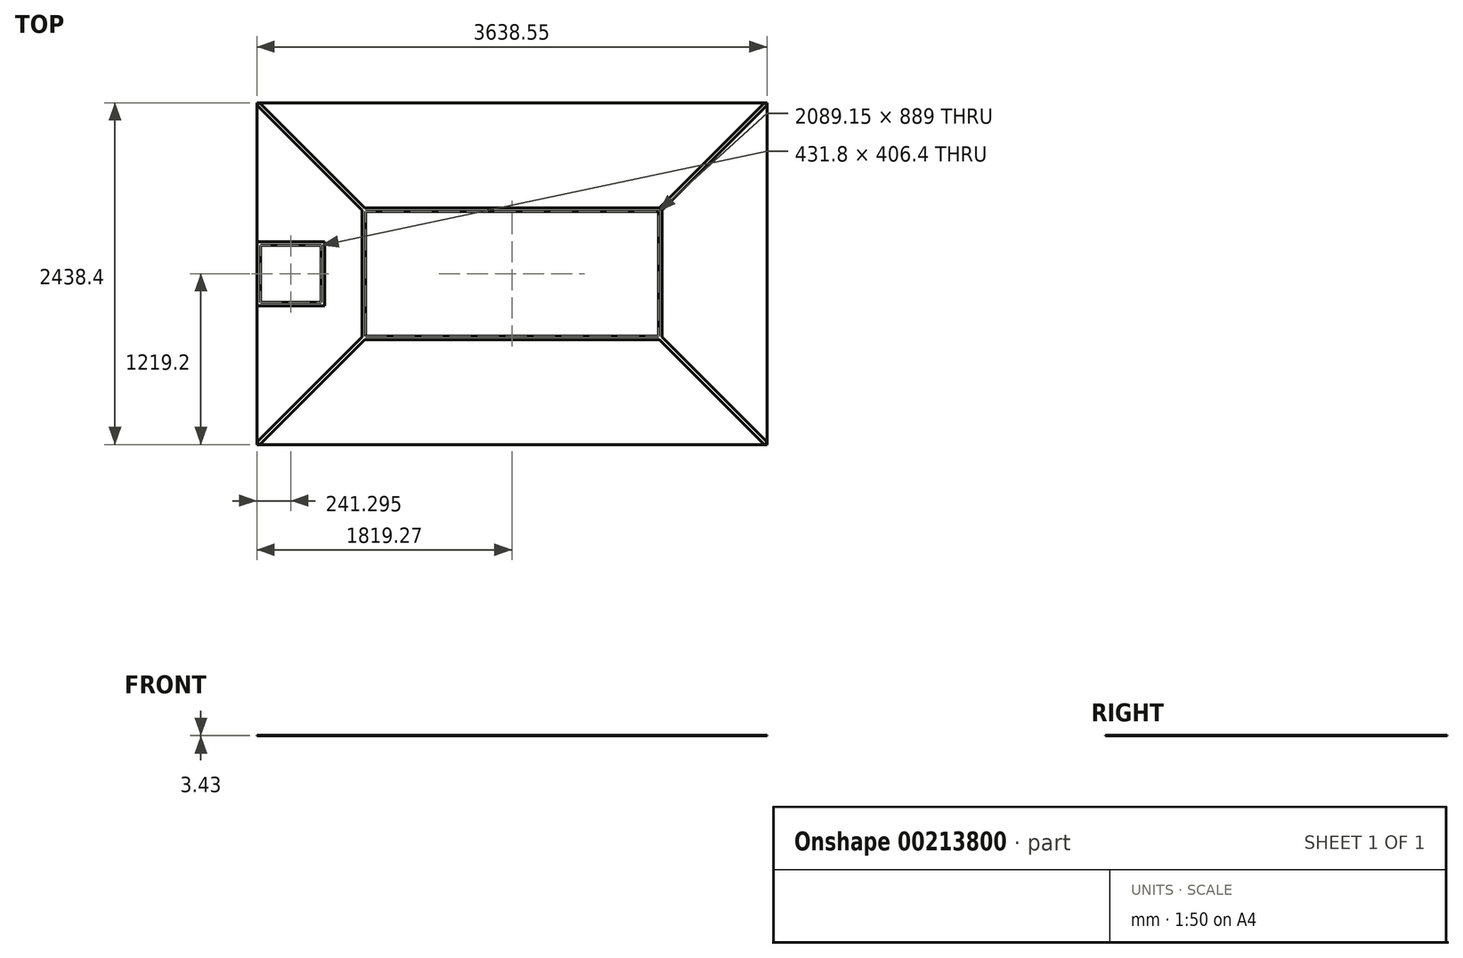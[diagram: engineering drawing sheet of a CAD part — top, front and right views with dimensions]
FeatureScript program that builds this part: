
annotation { "Feature Type Name" : "Feature", "Feature Type Description" : "" }
export const myFeature = defineFeature(function(context is Context, id is Id, definition is map)
    precondition{}
    {
        {
            var Q0;
            Q0=qCreatedBy(makeId("Top.planeOp"),FACE);
            var sketch = newSketch(context, id + "F0", { "sketchPlane" : qUnion([Q0])});
            skLineSegment(sketch, "E0.bottom", {"start": v(1819.27, 1219.2) * mm, "end": v(-1819.28, 1219.2) * mm});
            skLineSegment(sketch, "E0.top", {"start": v(1819.28, -1219.2) * mm, "end": v(-1819.28, -1219.2) * mm});
            skLineSegment(sketch, "E0.left", {"start": v(1819.28, 1219.2) * mm, "end": v(1819.28, -1219.2) * mm});
            skLineSegment(sketch, "E0.right", {"start": v(-1819.27, 1219.2) * mm, "end": v(-1819.28, -1219.2) * mm});
            skPoint(sketch, "E0.middle", {"position": v(0, 0) * mm});
            skSolve(sketch);
        }
        {
            var Q0;
            Q0=qSketchRegion(id+"F0",true);
            extrude(context, id + "F1", {"entities" : qUnion([Q0]), "depth" : 3.17 * mm});
        }
        {
            var Q0;
            Q0=makeQuery(id+"F1.opExtrude","CAP_FACE",FACE,{"disambiguationData":[OSD([sQuery(id+"F0.wireOp",EDGE,"E0.bottom"),sQuery(id+"F0.wireOp",EDGE,"E0.top"),sQuery(id+"F0.wireOp",EDGE,"E0.left"),sQuery(id+"F0.wireOp",EDGE,"E0.right")])],"isStart":false});
            var sketch = newSketch(context, id + "F2", { "sketchPlane" : qUnion([Q0])});
            skLineSegment(sketch, "E1.bottom", {"start": v(-1336.68, -228.6) * mm, "end": v(-1819.28, -228.6) * mm});
            skLineSegment(sketch, "E1.top", {"start": v(-1336.67, 228.6) * mm, "end": v(-1819.28, 228.6) * mm});
            skLineSegment(sketch, "E1.left", {"start": v(-1336.67, -228.6) * mm, "end": v(-1336.67, 228.6) * mm});
            skPoint(sketch, "E1.middle", {"position": v(-1819.28, 0) * mm});
            skPoint(sketch, "E2.orphan", {"position": v(-2301.88, 228.6) * mm});
            skPoint(sketch, "E3.orphan", {"position": v(-2301.88, -228.6) * mm});
            skLineSegment(sketch, "E4", {"start": v(-1819.28, 228.6) * mm, "end": v(-1819.28, -228.6) * mm});
            skLineSegment(sketch, "E5.0", {"start": v(-1362.08, 203.2) * mm, "end": v(-1793.88, 203.2) * mm});
            skLineSegment(sketch, "E5.1", {"start": v(-1362.08, -203.2) * mm, "end": v(-1362.08, 203.2) * mm});
            skLineSegment(sketch, "E5.2", {"start": v(-1362.08, -203.2) * mm, "end": v(-1793.88, -203.2) * mm});
            skLineSegment(sketch, "E5.3", {"start": v(-1793.88, 203.2) * mm, "end": v(-1793.88, -203.2) * mm});
            skSolve(sketch);
        }
        {
            var Q0;
            {var subQ4=sQuery(id+"F2.wireOp",EDGE,"E1.bottom");Q0=makeQuery(id+"F2.imprint","IMPRINT",FACE,{"disambiguationData":[TD([[makeQuery(id+"F2.imprint","IMPRINT",EDGE,{"derivedFrom":subQ4}),-1.0]])]});}
            extrude(context, id + "F3", {"entities" : qUnion([Q0]), "depth" : 0.25 * mm});
        }
        {
            var Q0;
            Q0=makeQuery(id+"F1.opExtrude","CAP_FACE",FACE,{"disambiguationData":[OSD([sQuery(id+"F0.wireOp",EDGE,"E0.bottom"),sQuery(id+"F0.wireOp",EDGE,"E0.top"),sQuery(id+"F0.wireOp",EDGE,"E0.left"),sQuery(id+"F0.wireOp",EDGE,"E0.right")])],"isStart":false});
            var sketch = newSketch(context, id + "F4", { "sketchPlane" : qUnion([Q0])});
            skLineSegment(sketch, "E6.bottom", {"start": v(-1057.28, 457.2) * mm, "end": v(1057.28, 457.2) * mm, "construction": true});
            skLineSegment(sketch, "E6.top", {"start": v(-1057.28, -457.2) * mm, "end": v(1057.28, -457.2) * mm, "construction": true});
            skLineSegment(sketch, "E6.left", {"start": v(-1057.28, 457.2) * mm, "end": v(-1057.28, -457.2) * mm, "construction": true});
            skLineSegment(sketch, "E6.right", {"start": v(1057.27, 457.2) * mm, "end": v(1057.27, -457.2) * mm, "construction": true});
            skPoint(sketch, "E6.middle", {"position": v(0, 0) * mm});
            skLineSegment(sketch, "E7", {"start": v(-1819.28, 1219.2) * mm, "end": v(-1057.27, 457.2) * mm, "construction": true});
            skLineSegment(sketch, "E8", {"start": v(-1819.28, -1219.2) * mm, "end": v(-1057.28, -457.2) * mm, "construction": true});
            skLineSegment(sketch, "E9", {"start": v(1819.28, -1219.2) * mm, "end": v(1057.28, -457.2) * mm, "construction": true});
            skLineSegment(sketch, "E10", {"start": v(1819.27, 1219.2) * mm, "end": v(1057.27, 457.2) * mm, "construction": true});
            skLineSegment(sketch, "E11.0", {"start": v(-1069.98, 451.94) * mm, "end": v(-1069.98, -451.94) * mm});
            skLineSegment(sketch, "E12.0", {"start": v(-1044.58, 444.5) * mm, "end": v(-1044.58, -444.5) * mm});
            skLineSegment(sketch, "E13.0", {"start": v(-1052.01, -469.9) * mm, "end": v(1052.01, -469.9) * mm});
            skLineSegment(sketch, "E14.0", {"start": v(-1044.58, -444.5) * mm, "end": v(1044.57, -444.5) * mm});
            skLineSegment(sketch, "E15.0", {"start": v(1044.58, 444.5) * mm, "end": v(1044.58, -444.5) * mm});
            skLineSegment(sketch, "E16.0", {"start": v(1069.97, 451.94) * mm, "end": v(1069.97, -451.94) * mm});
            skLineSegment(sketch, "E17.0", {"start": v(-1044.58, 444.5) * mm, "end": v(1044.57, 444.5) * mm});
            skLineSegment(sketch, "E18.0", {"start": v(-1052.01, 469.9) * mm, "end": v(1052.01, 469.9) * mm});
            skLineSegment(sketch, "E19.0", {"start": v(-1819.28, 1201.24) * mm, "end": v(-1069.98, 451.94) * mm});
            skLineSegment(sketch, "E20.0", {"start": v(-1801.31, 1219.2) * mm, "end": v(-1052.01, 469.9) * mm});
            skLineSegment(sketch, "E21.0", {"start": v(-1801.31, -1219.2) * mm, "end": v(-1052.01, -469.9) * mm});
            skLineSegment(sketch, "E22.0", {"start": v(-1819.28, -1201.24) * mm, "end": v(-1069.97, -451.94) * mm});
            skLineSegment(sketch, "E23.0", {"start": v(1819.28, -1201.24) * mm, "end": v(1069.97, -451.94) * mm});
            skLineSegment(sketch, "E24.0", {"start": v(1801.31, -1219.2) * mm, "end": v(1052.01, -469.9) * mm});
            skLineSegment(sketch, "E25.0", {"start": v(1801.31, 1219.2) * mm, "end": v(1052.01, 469.9) * mm});
            skLineSegment(sketch, "E26.0", {"start": v(1819.28, 1201.24) * mm, "end": v(1069.97, 451.94) * mm});
            skLineSegment(sketch, "E27.0", {"start": v(1819.27, 1219.2) * mm, "end": v(-1819.28, 1219.2) * mm});
            skLineSegment(sketch, "E28.0", {"start": v(1819.28, 1219.2) * mm, "end": v(1819.28, -1219.2) * mm});
            skLineSegment(sketch, "E29", {"start": v(1801.31, 1219.2) * mm, "end": v(1819.28, 1201.24) * mm});
            skLineSegment(sketch, "E30.0", {"start": v(1819.28, -1219.2) * mm, "end": v(-1819.28, -1219.2) * mm});
            skLineSegment(sketch, "E31", {"start": v(1801.31, -1219.2) * mm, "end": v(1819.28, -1201.24) * mm});
            skLineSegment(sketch, "E32.0", {"start": v(-1819.27, 1219.2) * mm, "end": v(-1819.28, -1219.2) * mm});
            skLineSegment(sketch, "E33", {"start": v(-1819.28, -1201.24) * mm, "end": v(-1801.31, -1219.2) * mm});
            skLineSegment(sketch, "E34", {"start": v(-1819.28, 1201.24) * mm, "end": v(-1801.31, 1219.2) * mm});
            skSolve(sketch);
        }
        {
            var Q0;
            Q0=makeQuery(id+"F4.imprint","IMPRINT",FACE,{"disambiguationData":[TD([[makeQuery(id+"F4.imprint","IMPRINT",EDGE,{"derivedFrom":sQuery(id+"F4.wireOp",EDGE,"E11.0")}),1.0]])]});
            extrude(context, id + "F5", {"entities" : qUnion([Q0]), "depth" : 0.25 * mm});
        }
    });
